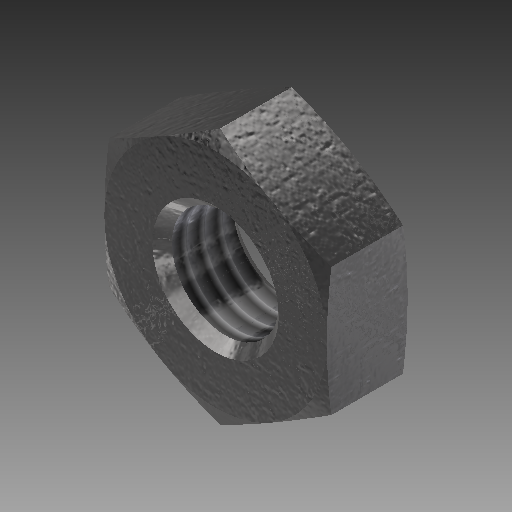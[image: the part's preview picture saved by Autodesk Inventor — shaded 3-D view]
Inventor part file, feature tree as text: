
AUTODESK INVENTOR PART (.ipt)
format: ipt  version: 2017 (Build 210142000, 142)  size: 267,776 bytes
history: native  units: in
note: dims shown in document units (in); Inventor stores cm internally (conversion verified against a paired STEP export)
features: other x70, sketch x3, revolve x2, extrude x1, thread x1
ambient origin geometry x8: Origin, YZ Plane, XZ Plane, XY Plane, X Axis, Y Axis, Z Axis, Center Point
bodies: Solid1 (feature_tree)
feature tree (77):
  sketch  "Sketch_8"  dims[d0=360.0deg d1=0.16in d2=0.0in]
  sketch  "Sketch_10"  dims[d3=360.0deg d4=0.1213in d5=0.0in]
  revolve  "Revolution1"  [1 undecoded]
  extrude  "Extrusion1"  Depth=0.1213in TaperAngle=0.0deg
  revolve  "Revolution2"  [1 undecoded]
  thread  "Thread1"  [1 undecoded]
  other  "NUT_XY"
  other  "NUT_YZ"
  other  "NUT_ZX"
  other  "NUT_X"
  other  "NUT_Y"
  other  "NUT_Z"
  other  "NUT_Center"
  other  "a1_XY"
  other  "a1_YZ"
  other  "a1_ZX"
  other  "a1_X"
  other  "a1_Y"
  other  "a1_Z"
  other  "a1_Center"
  other  "a2_XY"
  other  "a2_YZ"
  other  "a2_ZX"
  other  "a2_X"
  other  "a2_Y"
  other  "a2_Z"
  other  "a2_Center"
  other  "b1_XY"
  other  "b1_YZ"
  other  "b1_ZX"
  other  "b1_X"
  other  "b1_Y"
  other  "b1_Z"
  other  "b1_Center"
  other  "b2_XY"
  other  "b2_YZ"
  other  "b2_ZX"
  other  "b2_X"
  other  "b2_Y"
  other  "b2_Z"
  other  "b2_Center"
  other  "e_XY"
  other  "e_YZ"
  other  "e_ZX"
  other  "e_X"
  other  "e_Y"
  other  "e_Z"
  other  "e_Center"
  other  "ol1_XY"
  other  "ol1_YZ"
  other  "ol1_ZX"
  other  "ol1_X"
  other  "ol1_Y"
  other  "ol1_Z"
  other  "ol1_Center"
  other  "ol2_XY"
  other  "ol2_YZ"
  other  "ol2_ZX"
  other  "ol2_X"
  other  "ol2_Y"
  other  "ol2_Z"
  other  "ol2_Center"
  other  "th1_XY"
  other  "th1_YZ"
  other  "th1_ZX"
  other  "th1_X"
  other  "th1_Y"
  other  "th1_Z"
  other  "th1_Center"
  other  "th2_XY"
  other  "th2_YZ"
  other  "th2_ZX"
  other  "th2_X"
  other  "th2_Y"
  other  "th2_Z"
  other  "th2_Center"
  sketch  "Sketch_11"  dims[d6=0.0in]
note: 3 required parameter values undecoded (feature->parameter linkage not recoverable at this tier; creation-order binding heuristic only, values carry confidence <= 0.55)